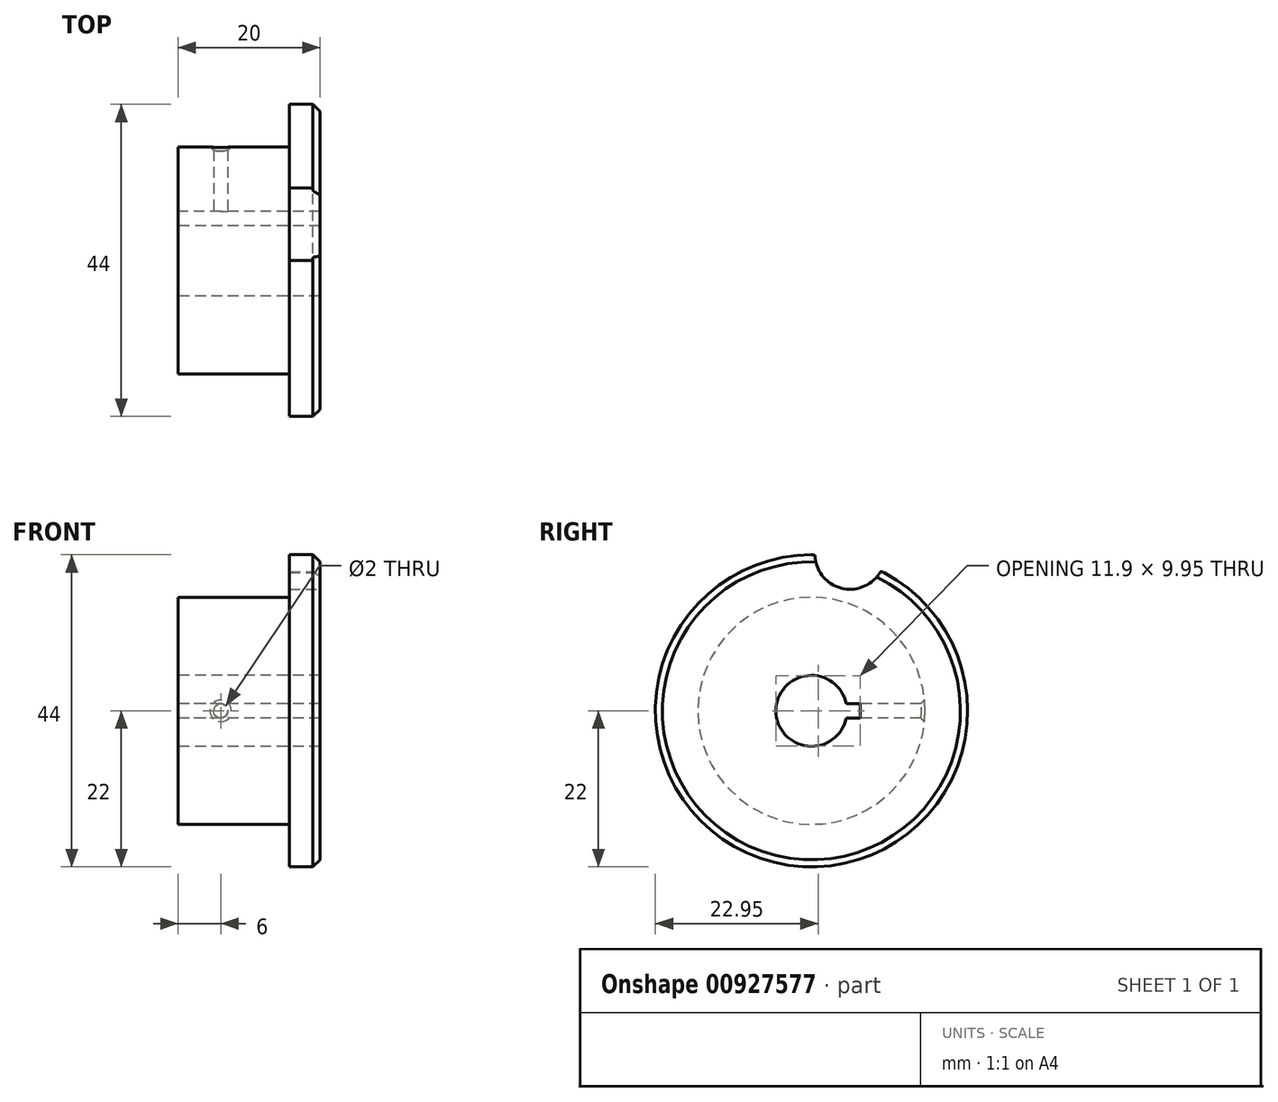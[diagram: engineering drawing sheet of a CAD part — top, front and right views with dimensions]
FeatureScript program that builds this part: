
annotation { "Feature Type Name" : "Feature", "Feature Type Description" : "" }
export const myFeature = defineFeature(function(context is Context, id is Id, definition is map)
    precondition{}
    {
        {
            var Q0;
            Q0=qCreatedBy(makeId("Right.planeOp"),FACE);
            var sketch = newSketch(context, id + "F0", { "sketchPlane" : qUnion([Q0])});
            skCircle(sketch, "E0", {"center": v(0, 0) * mm, "radius": 22 * mm});
            skSolve(sketch);
        }
        {
            var Q0;
            Q0=makeQuery(id+"F0.imprint","IMPRINT",FACE,{"disambiguationData":[TD([[makeQuery(id+"F0.imprint","IMPRINT",EDGE,{"derivedFrom":sQuery(id+"F0.wireOp",EDGE,"E0")}),1.0]])]});
            extrude(context, id + "F1", {"entities" : qUnion([Q0]), "oppositeDirection" : true, "depth" : 20 * mm, "offsetDistance" : 25 * mm});
        }
        {
            var Q0;
            Q0=makeQuery(id+"F1.opExtrude","CAP_FACE",FACE,{"disambiguationData":[OSD([sQuery(id+"F0.wireOp",EDGE,"E0")])],"isStart":false});
            var sketch = newSketch(context, id + "F2", { "sketchPlane" : qUnion([Q0])});
            skCircle(sketch, "E1", {"center": v(0, 0) * mm, "radius": 16 * mm});
            skSolve(sketch);
        }
        {
            var Q0;
            Q0=makeQuery(id+"F2.imprint","IMPRINT",FACE,{"disambiguationData":[TD([[makeQuery(id+"F2.imprint","IMPRINT",EDGE,{"derivedFrom":sQuery(id+"F2.wireOp",EDGE,"E1")}),-1.0]])]});
            extrude(context, id + "F3", {"entities" : qUnion([Q0]), "operationType" : NewBodyOperationType.REMOVE, "oppositeDirection" : true, "depth" : (20 - 4.3) * mm, "offsetDistance" : 25 * mm});
        }
        {
            var Q0;
            Q0=makeQuery(id+"F1.opExtrude","CAP_EDGE",EDGE,{"disambiguationData":[OSD([sQuery(id+"F0.wireOp",EDGE,"E0")])],"isStart":true});
            var Q1;
            Q1=makeQuery(id+"F3.boolean.opBoolean","COPY",EDGE,{"derivedFrom":makeQuery(id+"F3.opExtrude","CAP_EDGE",EDGE,{"disambiguationData":[OSD([sQuery(id+"F0.wireOp",EDGE,"E0")])],"isStart":false})});
            chamfer(context, id + "F4", {"entities" : qUnion([Q0, Q1]), "width" : 1 * mm, "tangentPropagation" : true});
        }
        {
            var Q0;
            Q0=makeQuery(id+"F1.opExtrude","CAP_FACE",FACE,{"disambiguationData":[OSD([sQuery(id+"F0.wireOp",EDGE,"E0")])],"isStart":true});
            var sketch = newSketch(context, id + "F5", { "sketchPlane" : qUnion([Q0])});
            skCircle(sketch, "E2", {"center": v(0, 0) * mm, "radius": 19.9 * mm, "construction": true});
            skCircle(sketch, "E3", {"center": v(0, 0) * mm, "radius": 17.8 * mm, "construction": true});
            skLineSegment(sketch, "E4", {"start": v(0, 30.58) * mm, "end": v(0, 0) * mm, "construction": true});
            skLineSegment(sketch, "E5", {"start": v(0, 0) * mm, "end": v(14.59, 27.8) * mm, "construction": true});
            skLineSegment(sketch, "E6", {"start": v(0, 0) * mm, "end": v(7.5, 30.4) * mm, "construction": true});
            skCircle(sketch, "E7", {"center": v(0, 0) * mm, "radius": 22 * mm});
            skLineSegment(sketch, "E8", {"start": v(0, 22) * mm, "end": v(0.3, 22) * mm});
            skLineSegment(sketch, "E9", {"start": v(10.22, 19.48) * mm, "end": v(9.95, 19.62) * mm});
            skArc(sketch, "E10", {"start": v(0.5, 21.8) * mm, "mid": v(4.26, 17.28) * mm, "end": v(9.68, 19.55) * mm});
            skPoint(sketch, "E11.visualSharp", {"position": v(9.78, 19.7) * mm});
            skArc(sketch, "E11.filletArc", {"start": v(9.95, 19.62) * mm, "mid": v(9.8, 19.64) * mm, "end": v(9.68, 19.55) * mm});
            skPoint(sketch, "E12.visualSharp", {"position": v(0.5, 22) * mm});
            skArc(sketch, "E12.filletArc", {"start": v(0.5, 21.8) * mm, "mid": v(0.45, 21.94) * mm, "end": v(0.3, 22) * mm});
            skSolve(sketch);
        }
        {
            var Q0;
            {var subQ0=sQuery(id+"F5.wireOp",EDGE,"E10");var subQ1=sQuery(id+"F5.wireOp",EDGE,"E7");var subQ2=makeQuery(id+"F5.imprint","INTERSECT",VERTEX,{"derivedFrom":[subQ1,sQuery(id+"F5.wireOp",EDGE,"E8"),subQ0]});Q0=makeQuery(id+"F5.imprint","IMPRINT",FACE,{"disambiguationData":[TD([[makeQuery(id+"F5.imprint","IMPRINT",EDGE,{"disambiguationData":[TD([[subQ2,1.0]])],"derivedFrom":subQ1}),1.0]])]});}
            var Q1;
            {var subQ0=sQuery(id+"F5.wireOp",EDGE,"E10");var subQ1=sQuery(id+"F0.wireOp",EDGE,"E0");var subQ2=makeQuery(id+"F4.opChamfer","BLEND_EDGE",EDGE,{"blendedFrom":[makeQuery(id+"F1.opExtrude","CAP_EDGE",EDGE,{"disambiguationData":[OSD([subQ1])],"isStart":true}),makeQuery(id+"F1.opExtrude","CAP_FACE",FACE,{"disambiguationData":[OSD([subQ1])],"isStart":true})],"blendedInto":[makeQuery(id+"F1.opExtrude","CAP_FACE",FACE,{"disambiguationData":[OSD([subQ1])],"isStart":true})]});var subQ3=makeQuery(id+"F5.imprint","INTERSECT",VERTEX,{"disambiguationData":[OD(0.0)],"derivedFrom":[subQ2,subQ0]});Q1=makeQuery(id+"F5.imprint","IMPRINT",FACE,{"disambiguationData":[TD([[makeQuery(id+"F5.imprint","IMPRINT",EDGE,{"disambiguationData":[TD([[subQ3,-1.0]])],"derivedFrom":subQ0}),1.0]])]});}
            extrude(context, id + "F6", {"entities" : qUnion([Q0, Q1]), "operationType" : NewBodyOperationType.REMOVE, "oppositeDirection" : true, "depth" : 25 * mm, "offsetDistance" : 25 * mm});
        }
        {
            var Q0;
            Q0=makeQuery(id+"F1.opExtrude","CAP_FACE",FACE,{"disambiguationData":[OSD([sQuery(id+"F0.wireOp",EDGE,"E0")])],"isStart":false});
            var sketch = newSketch(context, id + "F7", { "sketchPlane" : qUnion([Q0])});
            skArc(sketch, "E13", {"start": v(-4.9, -1) * mm, "mid": v(5, 0) * mm, "end": v(-4.9, 1) * mm});
            skLineSegment(sketch, "E14", {"start": v(-4.9, 1) * mm, "end": v(-6.9, 1) * mm});
            skLineSegment(sketch, "E15", {"start": v(-6.9, 1) * mm, "end": v(-6.9, -1) * mm});
            skLineSegment(sketch, "E16", {"start": v(-6.9, -1) * mm, "end": v(-4.9, -1) * mm});
            skSolve(sketch);
        }
        {
            var Q0;
            Q0 = qSketchRegion(id + "F7", true);
            extrude(context, id + "F8", {"entities" : qUnion([Q0]), "operationType" : NewBodyOperationType.REMOVE, "endBound" : BoundingType.THROUGH_ALL, "oppositeDirection" : true, "depth" : 25 * mm, "offsetDistance" : 25 * mm});
        }
        {
            var Q0;
            Q0=qCreatedBy(makeId("Front.planeOp"),FACE);
            var sketch = newSketch(context, id + "F9", { "sketchPlane" : qUnion([Q0])});
            skLineSegment(sketch, "E17", {"start": v(-46.33, 0) * mm, "end": v(25.8, 0) * mm, "construction": true});
            skLineSegment(sketch, "E18", {"start": v(-29.53, 16) * mm, "end": v(17.26, 16) * mm, "construction": true});
            skCircle(sketch, "E19", {"center": v(-14, 0) * mm, "radius": 1 * mm});
            skSolve(sketch);
        }
        {
            var Q0;
            Q0 = qSketchRegion(id + "F9", true);
            extrude(context, id + "F10", {"entities" : qUnion([Q0]), "operationType" : NewBodyOperationType.REMOVE, "endBound" : BoundingType.THROUGH_ALL, "oppositeDirection" : true, "depth" : 25 * mm, "offsetDistance" : 25 * mm});
        }
        {
            var Q0;
            Q0=makeQuery(id+"F10.boolean.opBoolean","INTERSECT",EDGE,{"derivedFrom":[makeQuery(id+"F3.boolean.opBoolean","COPY",FACE,{"derivedFrom":makeQuery(id+"F3.opExtrude","SWEPT_FACE",FACE,{"disambiguationData":[OSD([sQuery(id+"F2.wireOp",EDGE,"E1")])]})}),makeQuery(id+"F10.opExtrude","SWEPT_FACE",FACE,{"disambiguationData":[OSD([sQuery(id+"F9.wireOp",EDGE,"E19")])]})]});
            var Q1;
            Q1=makeQuery(id+"F5grBeGVlXW85Q4_1.1.F10.boolean.opBoolean","INTERSECT",EDGE,{"derivedFrom":[makeQuery(id+"F3.boolean.opBoolean","COPY",FACE,{"derivedFrom":makeQuery(id+"F3.opExtrude","SWEPT_FACE",FACE,{"disambiguationData":[OSD([sQuery(id+"F2.wireOp",EDGE,"E1")])]})}),makeQuery(id+"F5grBeGVlXW85Q4_1.1.F10.opExtrude","SWEPT_FACE",FACE,{"disambiguationData":[OSD([sQuery(id+"F9.wireOp",EDGE,"E19")])]})]});
            chamfer(context, id + "F11", {"entities" : qUnion([Q0, Q1]), "width" : 0.5 * mm, "tangentPropagation" : true});
        }
    });
